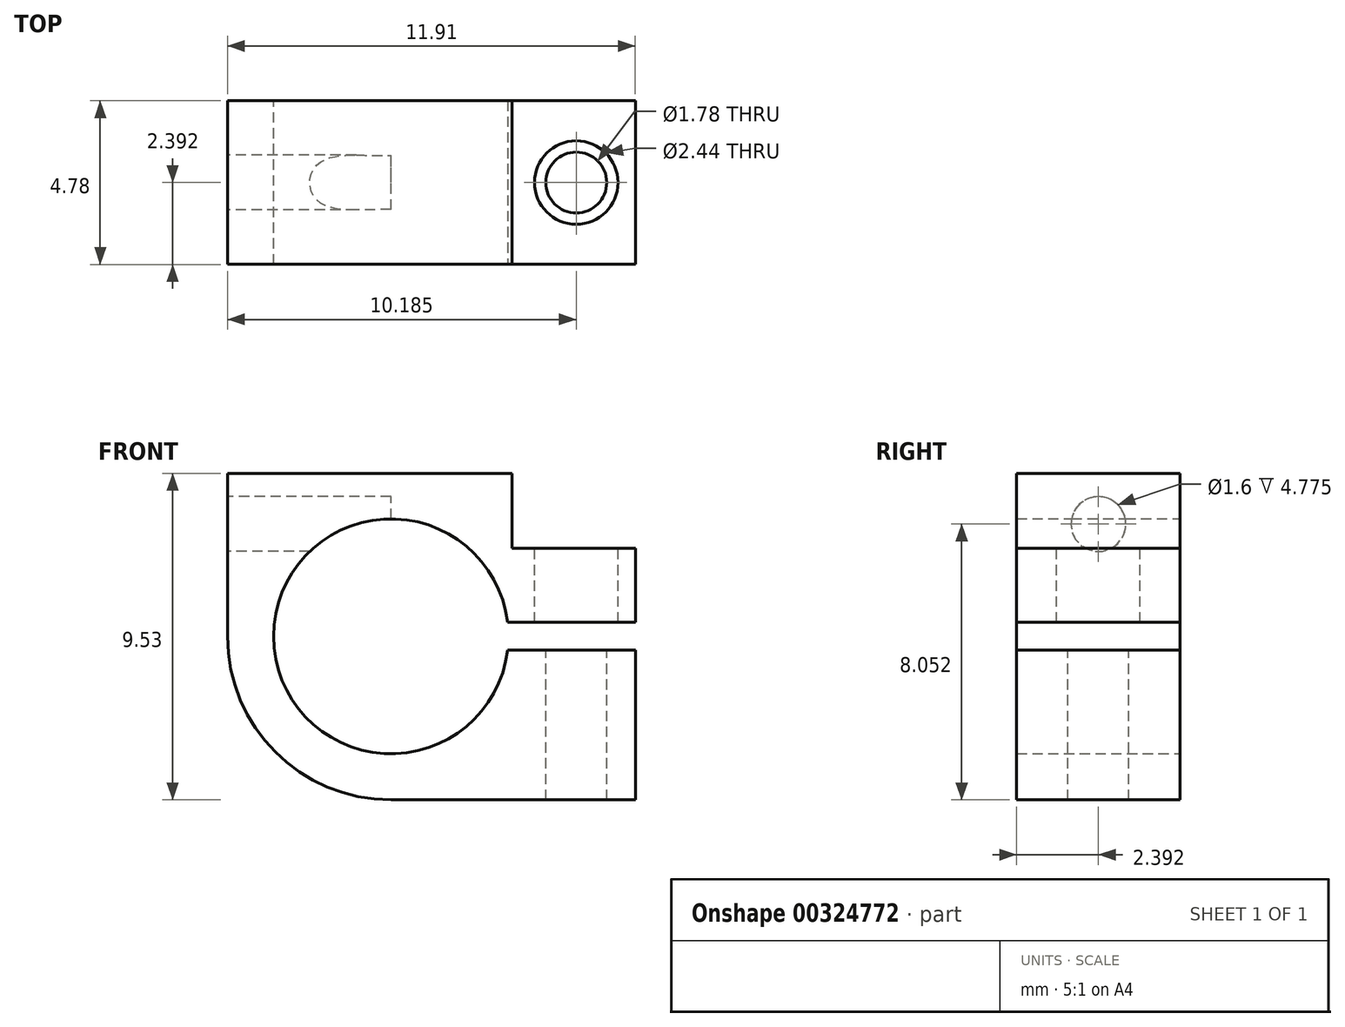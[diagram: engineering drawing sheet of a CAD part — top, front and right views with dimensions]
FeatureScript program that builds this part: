
annotation { "Feature Type Name" : "Feature", "Feature Type Description" : "" }
export const myFeature = defineFeature(function(context is Context, id is Id, definition is map)
    precondition{}
    {
        {
            var Q0;
            Q0=qCreatedBy(makeId("Front.planeOp"),FACE);
            var sketch = newSketch(context, id + "F0", { "sketchPlane" : qUnion([Q0])});
            skLineSegment(sketch, "E0.bottom", {"start": v(0, 0) * mm, "end": v(11.91, 0) * mm});
            skLineSegment(sketch, "E0.top", {"start": v(0, 9.53) * mm, "end": v(8.3, 9.53) * mm});
            skLineSegment(sketch, "E0.left", {"start": v(0, 0) * mm, "end": v(0, 9.53) * mm});
            skLineSegment(sketch, "E0.right", {"start": v(11.91, 0) * mm, "end": v(11.91, 7.34) * mm});
            skLineSegment(sketch, "E1", {"start": v(8.3, 9.53) * mm, "end": v(8.3, 7.34) * mm});
            skLineSegment(sketch, "E2", {"start": v(8.3, 7.34) * mm, "end": v(11.91, 7.34) * mm});
            skCircle(sketch, "E3", {"center": v(4.78, 4.78) * mm, "radius": 3.43 * mm});
            skSolve(sketch);
        }
        {
            var Q0;
            Q0=makeQuery(id+"F0.imprint","IMPRINT",FACE,{"disambiguationData":[TD([[makeQuery(id+"F0.imprint","IMPRINT",EDGE,{"derivedFrom":sQuery(id+"F0.wireOp",EDGE,"E0.bottom")}),1.0]])]});
            extrude(context, id + "F1", {"entities" : qUnion([Q0]), "depth" : 4.78 * mm, "offsetDistance" : 25.4 * mm});
        }
        {
            var Q0;
            Q0=makeQuery(id+"F1.opExtrude","CAP_FACE",FACE,{"disambiguationData":[OSD([sQuery(id+"F0.wireOp",EDGE,"E0.bottom"),sQuery(id+"F0.wireOp",EDGE,"E0.top"),sQuery(id+"F0.wireOp",EDGE,"E0.left"),sQuery(id+"F0.wireOp",EDGE,"E0.right"),sQuery(id+"F0.wireOp",EDGE,"E1"),sQuery(id+"F0.wireOp",EDGE,"E2"),sQuery(id+"F0.wireOp",EDGE,"E3")])],"isStart":false});
            var sketch = newSketch(context, id + "F2", { "sketchPlane" : qUnion([Q0])});
            skLineSegment(sketch, "E4.bottom", {"start": v(7.49, 5.18) * mm, "end": v(13.38, 5.18) * mm});
            skLineSegment(sketch, "E4.top", {"start": v(7.49, 4.37) * mm, "end": v(13.38, 4.37) * mm});
            skLineSegment(sketch, "E4.left", {"start": v(7.49, 5.18) * mm, "end": v(7.49, 4.37) * mm});
            skLineSegment(sketch, "E4.right", {"start": v(13.38, 5.18) * mm, "end": v(13.38, 4.37) * mm});
            skSolve(sketch);
        }
        {
            var Q0;
            {var subQ0=sQuery(id+"F2.wireOp",EDGE,"E4.bottom");var subQ1=makeQuery(id+"F1.opExtrude","CAP_EDGE",EDGE,{"disambiguationData":[OSD([sQuery(id+"F0.wireOp",EDGE,"E0.right")])],"isStart":false});var subQ2=makeQuery(id+"F2.imprint","INTERSECT",VERTEX,{"derivedFrom":[subQ1,subQ0]});Q0=makeQuery(id+"F2.imprint","IMPRINT",FACE,{"disambiguationData":[TD([[makeQuery(id+"F2.imprint","IMPRINT",EDGE,{"disambiguationData":[TD([[subQ2,1.0]])],"derivedFrom":subQ0}),-1.0]])]});}
            extrude(context, id + "F3", {"entities" : qUnion([Q0]), "operationType" : NewBodyOperationType.REMOVE, "endBound" : BoundingType.THROUGH_ALL, "oppositeDirection" : true, "depth" : 25.4 * mm, "offsetDistance" : 25.4 * mm});
        }
        {
            var Q0;
            Q0=makeQuery(id+"F1.opExtrude","SWEPT_FACE",FACE,{"disambiguationData":[OSD([sQuery(id+"F0.wireOp",EDGE,"E2")])]});
            var sketch = newSketch(context, id + "F4", { "sketchPlane" : qUnion([Q0])});
            skCircle(sketch, "E5", {"center": v(10.19, -2.39) * mm, "radius": 0.89 * mm});
            skSolve(sketch);
        }
        {
            var Q0;
            Q0=makeQuery(id+"F4.imprint","IMPRINT",FACE,{"disambiguationData":[TD([[makeQuery(id+"F4.imprint","IMPRINT",EDGE,{"derivedFrom":sQuery(id+"F4.wireOp",EDGE,"E5")}),1.0]])]});
            extrude(context, id + "F5", {"entities" : qUnion([Q0]), "operationType" : NewBodyOperationType.REMOVE, "endBound" : BoundingType.THROUGH_ALL, "oppositeDirection" : true, "depth" : 25.4 * mm, "offsetDistance" : 25.4 * mm});
        }
        {
            var Q0;
            Q0=makeQuery(id+"F1.opExtrude","SWEPT_FACE",FACE,{"disambiguationData":[OSD([sQuery(id+"F0.wireOp",EDGE,"E2")])]});
            var sketch = newSketch(context, id + "F6", { "sketchPlane" : qUnion([Q0])});
            skCircle(sketch, "E6", {"center": v(10.19, -2.39) * mm, "radius": 1.22 * mm});
            skSolve(sketch);
        }
        {
            var Q0;
            Q0=makeQuery(id+"F6.imprint","IMPRINT",FACE,{"disambiguationData":[TD([[makeQuery(id+"F6.imprint","IMPRINT",EDGE,{"derivedFrom":sQuery(id+"F6.wireOp",EDGE,"E6")}),1.0]])]});
            extrude(context, id + "F7", {"entities" : qUnion([Q0]), "operationType" : NewBodyOperationType.REMOVE, "oppositeDirection" : true, "depth" : 2.6 * mm, "offsetDistance" : 25.4 * mm});
        }
        {
            var Q0;
            Q0=makeQuery(id+"F1.opExtrude","SWEPT_FACE",FACE,{"disambiguationData":[OSD([sQuery(id+"F0.wireOp",EDGE,"E0.left")])]});
            var sketch = newSketch(context, id + "F8", { "sketchPlane" : qUnion([Q0])});
            skCircle(sketch, "E7", {"center": v(2.39, 8.05) * mm, "radius": 0.8 * mm});
            skSolve(sketch);
        }
        {
            var Q0;
            Q0=makeQuery(id+"F8.imprint","IMPRINT",FACE,{"disambiguationData":[TD([[makeQuery(id+"F8.imprint","IMPRINT",EDGE,{"derivedFrom":sQuery(id+"F8.wireOp",EDGE,"E7")}),1.0]])]});
            extrude(context, id + "F9", {"entities" : qUnion([Q0]), "operationType" : NewBodyOperationType.REMOVE, "oppositeDirection" : true, "depth" : 4.78 * mm, "offsetDistance" : 25.4 * mm});
        }
        {
            var Q0;
            Q0=makeQuery(id+"F1.opExtrude","SWEPT_EDGE",EDGE,{"disambiguationData":[OSD([sQuery(id+"F0.wireOp",EDGE,"E0.bottom"),sQuery(id+"F0.wireOp",EDGE,"E0.left")])]});
            fillet(context, id + "F10", {"entities" : qUnion([Q0]), "tangentPropagation" : true, "radius" : 4.78 * mm, "defaultsChanged" : true, "vertexSettings" : [], "allowEdgeOverflow" : false});
        }
    });
